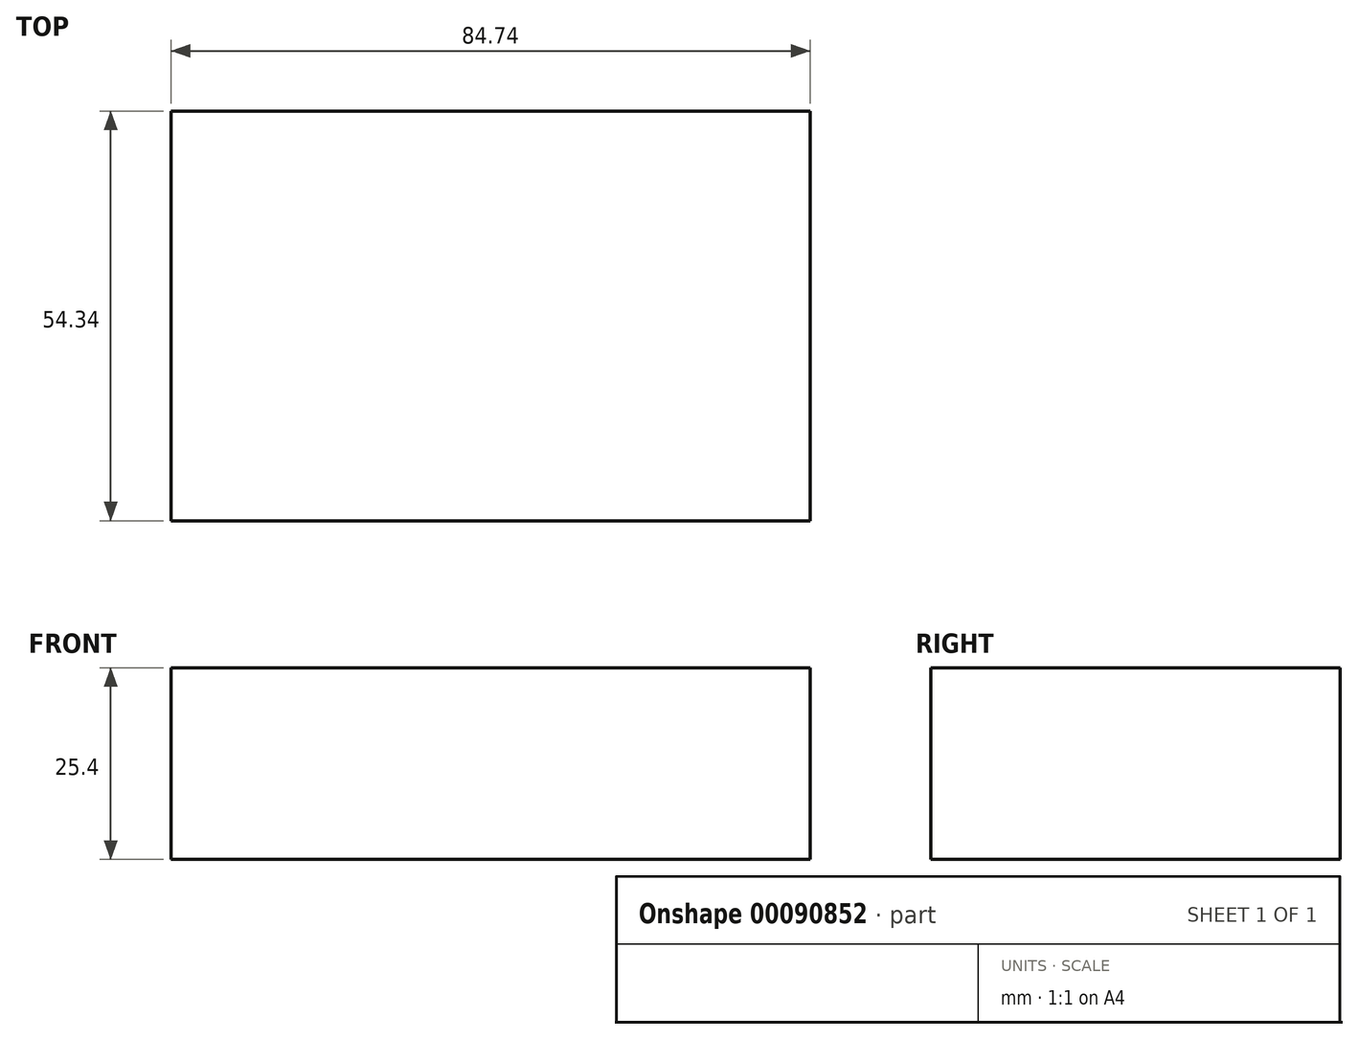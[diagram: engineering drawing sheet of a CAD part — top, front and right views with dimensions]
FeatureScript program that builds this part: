
annotation { "Feature Type Name" : "Feature", "Feature Type Description" : "" }
export const myFeature = defineFeature(function(context is Context, id is Id, definition is map)
    precondition{}
    {
        {
            var Q0;
            Q0=qCreatedBy(makeId("Top.planeOp"),FACE);
            var sketch = newSketch(context, id + "F0", { "sketchPlane" : qUnion([Q0])});
            skLineSegment(sketch, "E0.bottom", {"start": v(-36.95, -9.28) * mm, "end": v(47.8, -9.28) * mm});
            skLineSegment(sketch, "E0.top", {"start": v(-36.95, -63.62) * mm, "end": v(47.8, -63.62) * mm});
            skLineSegment(sketch, "E0.left", {"start": v(-36.95, -9.28) * mm, "end": v(-36.95, -63.62) * mm});
            skLineSegment(sketch, "E0.right", {"start": v(47.8, -9.28) * mm, "end": v(47.8, -63.62) * mm});
            skSolve(sketch);
        }
        {
            var Q0;
            Q0=makeQuery(id+"F0.imprint","IMPRINT",FACE,{"disambiguationData":[TD([[makeQuery(id+"F0.imprint","IMPRINT",EDGE,{"derivedFrom":sQuery(id+"F0.wireOp",EDGE,"E0.bottom")}),-1.0]])]});
            extrude(context, id + "F1", {"entities" : qUnion([Q0]), "depth" : 25.4 * mm});
        }
    });
